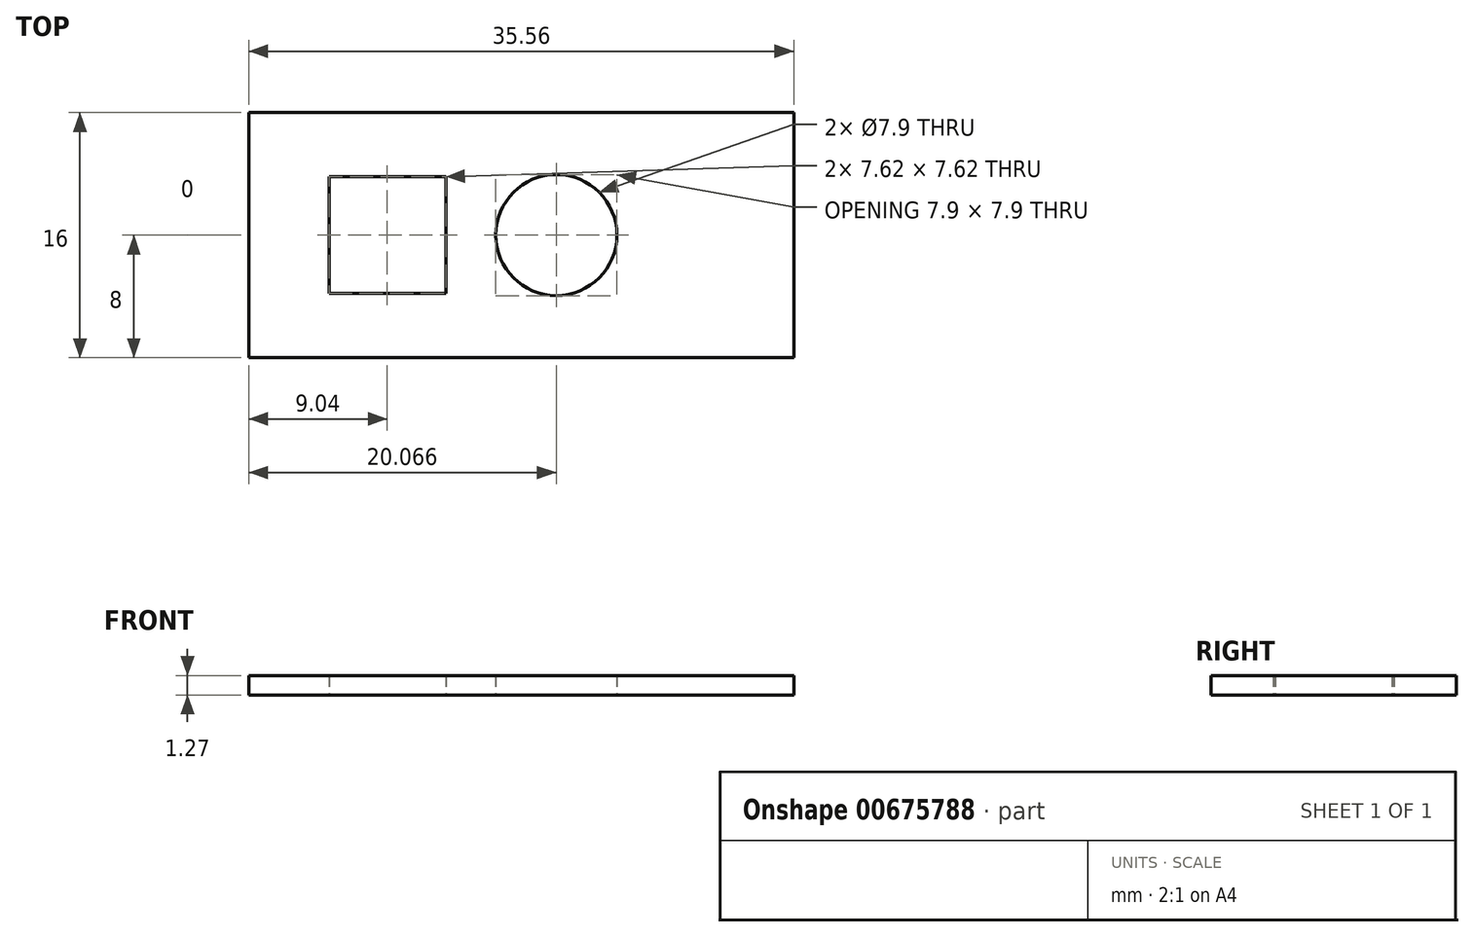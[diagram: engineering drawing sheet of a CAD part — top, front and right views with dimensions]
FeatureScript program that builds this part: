
annotation { "Feature Type Name" : "Feature", "Feature Type Description" : "" }
export const myFeature = defineFeature(function(context is Context, id is Id, definition is map)
    precondition{}
    {
        {
            var Q0;
            Q0=qCreatedBy(makeId("Top.planeOp"),FACE);
            var sketch = newSketch(context, id + "F0", { "sketchPlane" : qUnion([Q0])});
            skLineSegment(sketch, "E0.bottom", {"start": v(17.78, 8) * mm, "end": v(-17.78, 8) * mm});
            skLineSegment(sketch, "E0.top", {"start": v(17.78, -8) * mm, "end": v(-17.78, -8) * mm});
            skLineSegment(sketch, "E0.left", {"start": v(17.78, 8) * mm, "end": v(17.78, -8) * mm});
            skLineSegment(sketch, "E0.right", {"start": v(-17.78, 8) * mm, "end": v(-17.78, -8) * mm});
            skPoint(sketch, "E0.middle", {"position": v(0, 0) * mm});
            skSolve(sketch);
        }
        {
            var Q0;
            Q0=qSketchRegion(id+"F0",true);
            extrude(context, id + "F1", {"entities" : qUnion([Q0]), "depth" : 1.27 * mm, "offsetDistance" : 25.4 * mm});
        }
        {
            var Q0;
            Q0=makeQuery(id+"F1.opExtrude","CAP_FACE",FACE,{"disambiguationData":[OSD([sQuery(id+"F0.wireOp",EDGE,"E0.bottom"),sQuery(id+"F0.wireOp",EDGE,"E0.top"),sQuery(id+"F0.wireOp",EDGE,"E0.left"),sQuery(id+"F0.wireOp",EDGE,"E0.right")])],"isStart":true});
            var sketch = newSketch(context, id + "F2", { "sketchPlane" : qUnion([Q0])});
            skLineSegment(sketch, "E1", {"start": v(-17.78, 0) * mm, "end": v(-8.74, 0) * mm});
            skPoint(sketch, "E1.endSnap0", {"position": v(-17.78, 0) * mm});
            skLineSegment(sketch, "E2.bottom", {"start": v(-12.55, 3.81) * mm, "end": v(-4.93, 3.81) * mm});
            skLineSegment(sketch, "E2.top", {"start": v(-12.55, -3.8) * mm, "end": v(-4.93, -3.8) * mm});
            skLineSegment(sketch, "E2.left", {"start": v(-12.55, 3.81) * mm, "end": v(-12.55, -3.8) * mm});
            skLineSegment(sketch, "E2.right", {"start": v(-4.93, 3.81) * mm, "end": v(-4.93, -3.8) * mm});
            skPoint(sketch, "E2.middle", {"position": v(-8.74, 0) * mm});
            skLineSegment(sketch, "E3", {"start": v(-17.78, 0) * mm, "end": v(2.29, 0) * mm});
            skPoint(sketch, "E3.endSnap0", {"position": v(-12.55, 0) * mm});
            skCircle(sketch, "E4", {"center": v(2.29, 0) * mm, "radius": 3.95 * mm});
            skSolve(sketch);
        }
        {
            var Q0;
            Q0=sQuery(id+"F2.wireOp",VERTEX,"E3.end");
            var Q1;
            Q1=makeQuery(id+"F1.opExtrude","SWEPT_BODY",BODY,{"disambiguationData":[OSD([sQuery(id+"F0.wireOp",EDGE,"E0.bottom"),sQuery(id+"F0.wireOp",EDGE,"E0.top"),sQuery(id+"F0.wireOp",EDGE,"E0.left"),sQuery(id+"F0.wireOp",EDGE,"E0.right")])]});
            hole(context, id + "F3", {"style" : HoleStyle.SIMPLE, "endStyle" : HoleEndStyle.THROUGH, "holeDiameter" : 7.9 * mm, "locations" : qUnion([Q0]), "scope" : qUnion([Q1]), "isTappedThrough" : true});
        }
        {
            var Q0;
            {var subQ5=sQuery(id+"F2.wireOp",EDGE,"E2.bottom");Q0=makeQuery(id+"F2.imprint","IMPRINT",FACE,{"disambiguationData":[TD([[makeQuery(id+"F2.imprint","IMPRINT",EDGE,{"derivedFrom":subQ5}),-1.0]])]});}
            var Q1;
            {var subQ5=sQuery(id+"F2.wireOp",EDGE,"E2.top");Q1=makeQuery(id+"F2.imprint","IMPRINT",FACE,{"disambiguationData":[TD([[makeQuery(id+"F2.imprint","IMPRINT",EDGE,{"derivedFrom":subQ5}),1.0]])]});}
            extrude(context, id + "F4", {"entities" : qUnion([Q0, Q1]), "operationType" : NewBodyOperationType.REMOVE, "endBound" : BoundingType.THROUGH_ALL, "oppositeDirection" : true, "depth" : 25.4 * mm});
        }
    });
